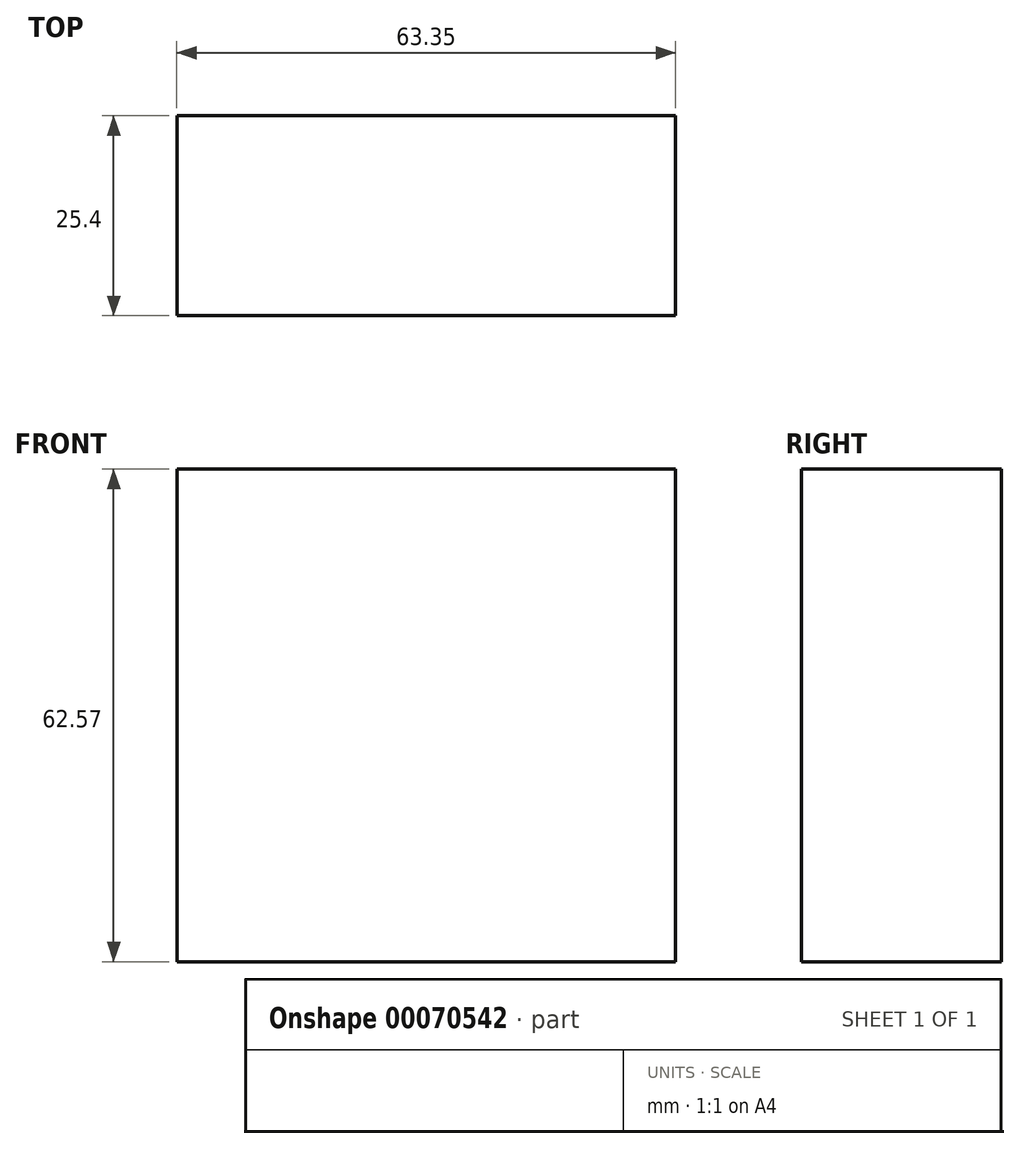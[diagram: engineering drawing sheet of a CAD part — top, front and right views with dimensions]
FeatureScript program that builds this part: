
annotation { "Feature Type Name" : "Feature", "Feature Type Description" : "" }
export const myFeature = defineFeature(function(context is Context, id is Id, definition is map)
    precondition{}
    {
        {
            var Q0;
            Q0=qCreatedBy(makeId("Front.planeOp"),FACE);
            var sketch = newSketch(context, id + "F0", { "sketchPlane" : qUnion([Q0])});
            skLineSegment(sketch, "E0.bottom", {"start": v(-27.16, 30.9) * mm, "end": v(36.2, 30.9) * mm});
            skLineSegment(sketch, "E0.top", {"start": v(-27.16, -31.66) * mm, "end": v(36.2, -31.66) * mm});
            skLineSegment(sketch, "E0.left", {"start": v(-27.16, 30.9) * mm, "end": v(-27.16, -31.66) * mm});
            skLineSegment(sketch, "E0.right", {"start": v(36.2, 30.9) * mm, "end": v(36.2, -31.66) * mm});
            skSolve(sketch);
        }
        {
            var Q0;
            Q0=makeQuery(id+"F0.imprint","IMPRINT",FACE,{"disambiguationData":[TD([[makeQuery(id+"F0.imprint","IMPRINT",EDGE,{"derivedFrom":sQuery(id+"F0.wireOp",EDGE,"E0.bottom")}),-1.0]])]});
            extrude(context, id + "F1", {"entities" : qUnion([Q0]), "depth" : 25.4 * mm});
        }
    });
